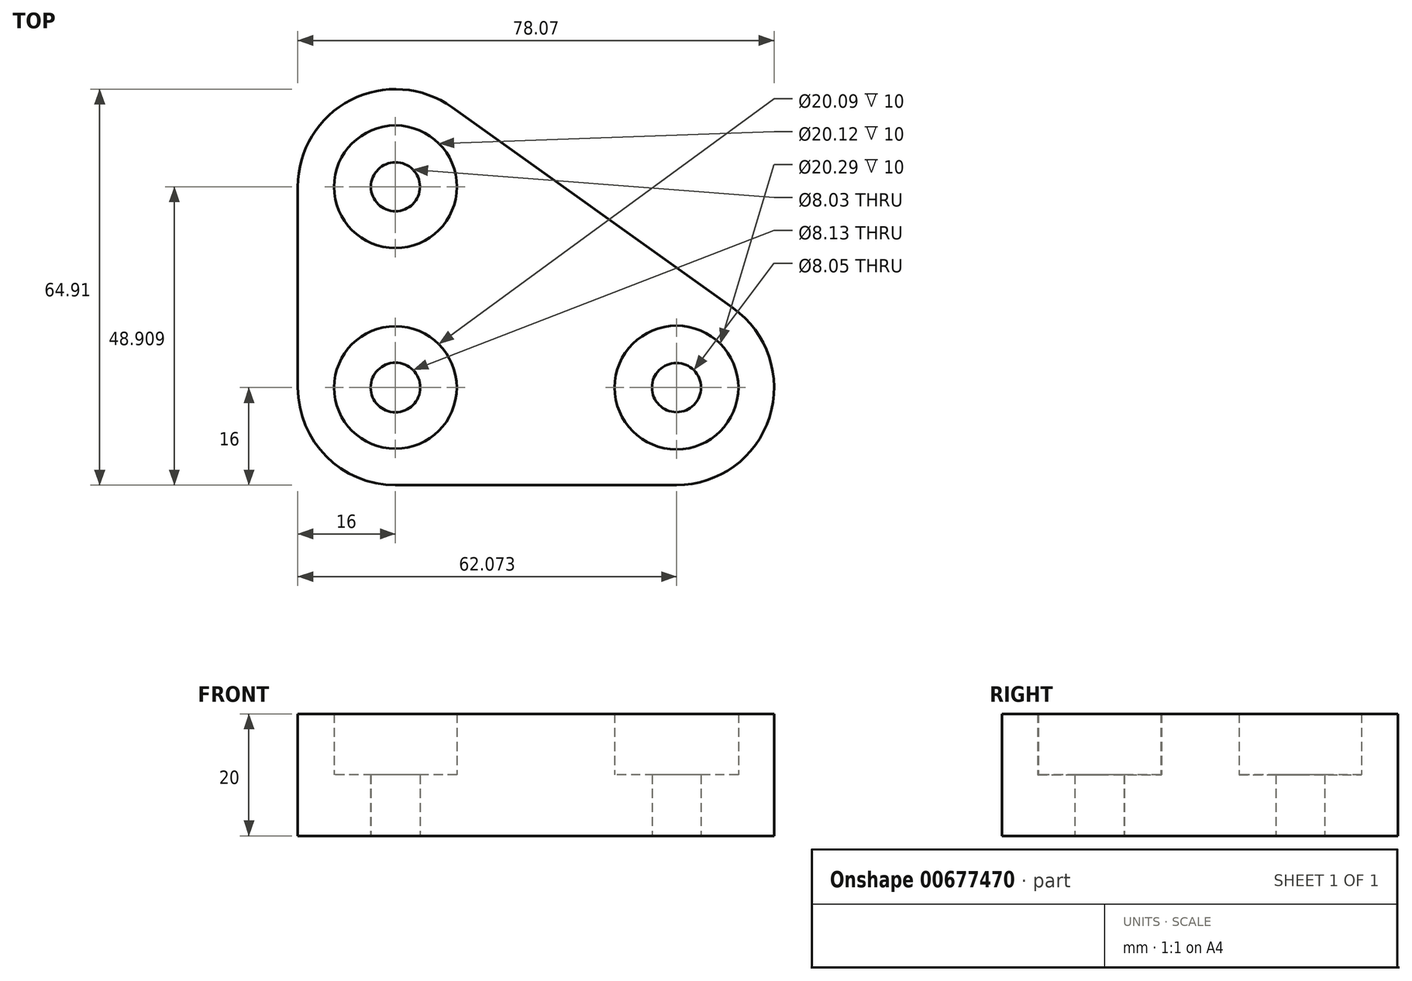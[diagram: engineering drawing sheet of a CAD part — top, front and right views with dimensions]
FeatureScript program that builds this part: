
annotation { "Feature Type Name" : "Feature", "Feature Type Description" : "" }
export const myFeature = defineFeature(function(context is Context, id is Id, definition is map)
    precondition{}
    {
        {
            var Q0;
            Q0=qCreatedBy(makeId("Top.planeOp"),FACE);
            var sketch = newSketch(context, id + "F0", { "sketchPlane" : qUnion([Q0])});
            skLineSegment(sketch, "E0.bottom", {"start": v(16, 0) * mm, "end": v(62.07, 0) * mm});
            skLineSegment(sketch, "E0.left", {"start": v(0, 16) * mm, "end": v(0, 48.9) * mm});
            skLineSegment(sketch, "E1", {"start": v(25.3, 61.93) * mm, "end": v(71.37, 29.02) * mm});
            skPoint(sketch, "E2.visualSharp", {"position": v(0, 80) * mm});
            skArc(sketch, "E2.filletArc", {"start": v(25.3, 61.93) * mm, "mid": v(8.68, 63.14) * mm, "end": v(0, 48.9) * mm});
            skPoint(sketch, "E3.visualSharp", {"position": v(0, 0) * mm});
            skArc(sketch, "E3.filletArc", {"start": v(0, 16) * mm, "mid": v(4.69, 4.69) * mm, "end": v(16, 0) * mm});
            skPoint(sketch, "E4.visualSharp", {"position": v(112, 0) * mm});
            skArc(sketch, "E4.filletArc", {"start": v(62.07, 0) * mm, "mid": v(77.3, 11.12) * mm, "end": v(71.37, 29.02) * mm});
            skCircle(sketch, "E5", {"center": v(16, 48.9) * mm, "radius": 4.02 * mm});
            skCircle(sketch, "E6", {"center": v(16, 16) * mm, "radius": 4.07 * mm});
            skCircle(sketch, "E7", {"center": v(62.07, 16) * mm, "radius": 4.03 * mm});
            skCircle(sketch, "E8", {"center": v(16, 48.9) * mm, "radius": 10.06 * mm});
            skCircle(sketch, "E9", {"center": v(16, 16) * mm, "radius": 10.05 * mm});
            skCircle(sketch, "E10", {"center": v(62.07, 16) * mm, "radius": 10.15 * mm});
            skSolve(sketch);
        }
        {
            var Q0;
            Q0=makeQuery(id+"F0.imprint","IMPRINT",FACE,{"disambiguationData":[TD([[makeQuery(id+"F0.imprint","IMPRINT",EDGE,{"derivedFrom":sQuery(id+"F0.wireOp",EDGE,"E0.bottom")}),1.0]])]});
            extrude(context, id + "F1", {"entities" : qUnion([Q0]), "depth" : 20 * mm, "offsetDistance" : 25 * mm});
        }
        {
            var Q0;
            Q0=makeQuery(id+"F0.imprint","IMPRINT",FACE,{"disambiguationData":[TD([[makeQuery(id+"F0.imprint","IMPRINT",EDGE,{"derivedFrom":sQuery(id+"F0.wireOp",EDGE,"E5")}),-1.0]])]});
            var Q1;
            Q1=makeQuery(id+"F0.imprint","IMPRINT",FACE,{"disambiguationData":[TD([[makeQuery(id+"F0.imprint","IMPRINT",EDGE,{"derivedFrom":sQuery(id+"F0.wireOp",EDGE,"E6")}),-1.0]])]});
            var Q2;
            Q2=makeQuery(id+"F0.imprint","IMPRINT",FACE,{"disambiguationData":[TD([[makeQuery(id+"F0.imprint","IMPRINT",EDGE,{"derivedFrom":sQuery(id+"F0.wireOp",EDGE,"E7")}),-1.0]])]});
            extrude(context, id + "F2", {"entities" : qUnion([Q0, Q1, Q2]), "operationType" : NewBodyOperationType.ADD, "depth" : 10 * mm, "offsetDistance" : 25 * mm});
        }
    });
